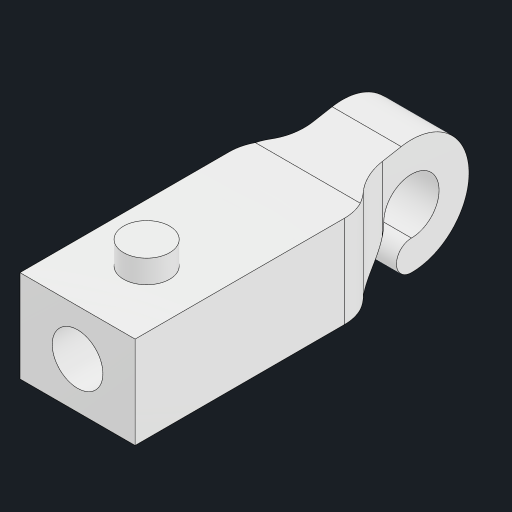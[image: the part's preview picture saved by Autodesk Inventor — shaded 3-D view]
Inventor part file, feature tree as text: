
AUTODESK INVENTOR PART (.ipt)
format: ipt  version: 2023 (Build 270158000, 158)  size: 162,304 bytes
history: native  units: mm
features: sketch x5, extrude x3, hole x2, other x1, fillet x1
ambient origin geometry x8: Origin, YZ Plane, XZ Plane, XY Plane, X Axis, Y Axis, Z Axis, Center Point
bodies: Body1 (feature_tree)
feature tree (12):
  other  "ソリッド1"
  extrude  "押し出し1"  Depth=5.0mm
  extrude  "押し出し2"  Depth=4.0mm TaperAngle=0.0deg
  hole  "加工用"  [1 undecoded]
  extrude  "押し出し4"  Depth=6.0mm TaperAngle=0.0deg
  fillet  "フィレット1"  Radius=10.0mm
  hole  "穴3"  [1 undecoded]
  sketch  "スケッチ1"
  sketch  "スケッチ2"
  sketch  "スケッチ5"
  sketch  "スケッチ6"
  sketch  "スケッチ8"
note: 2 required parameter values undecoded (feature->parameter linkage not recoverable at this tier; creation-order binding heuristic only, values carry confidence <= 0.55)
